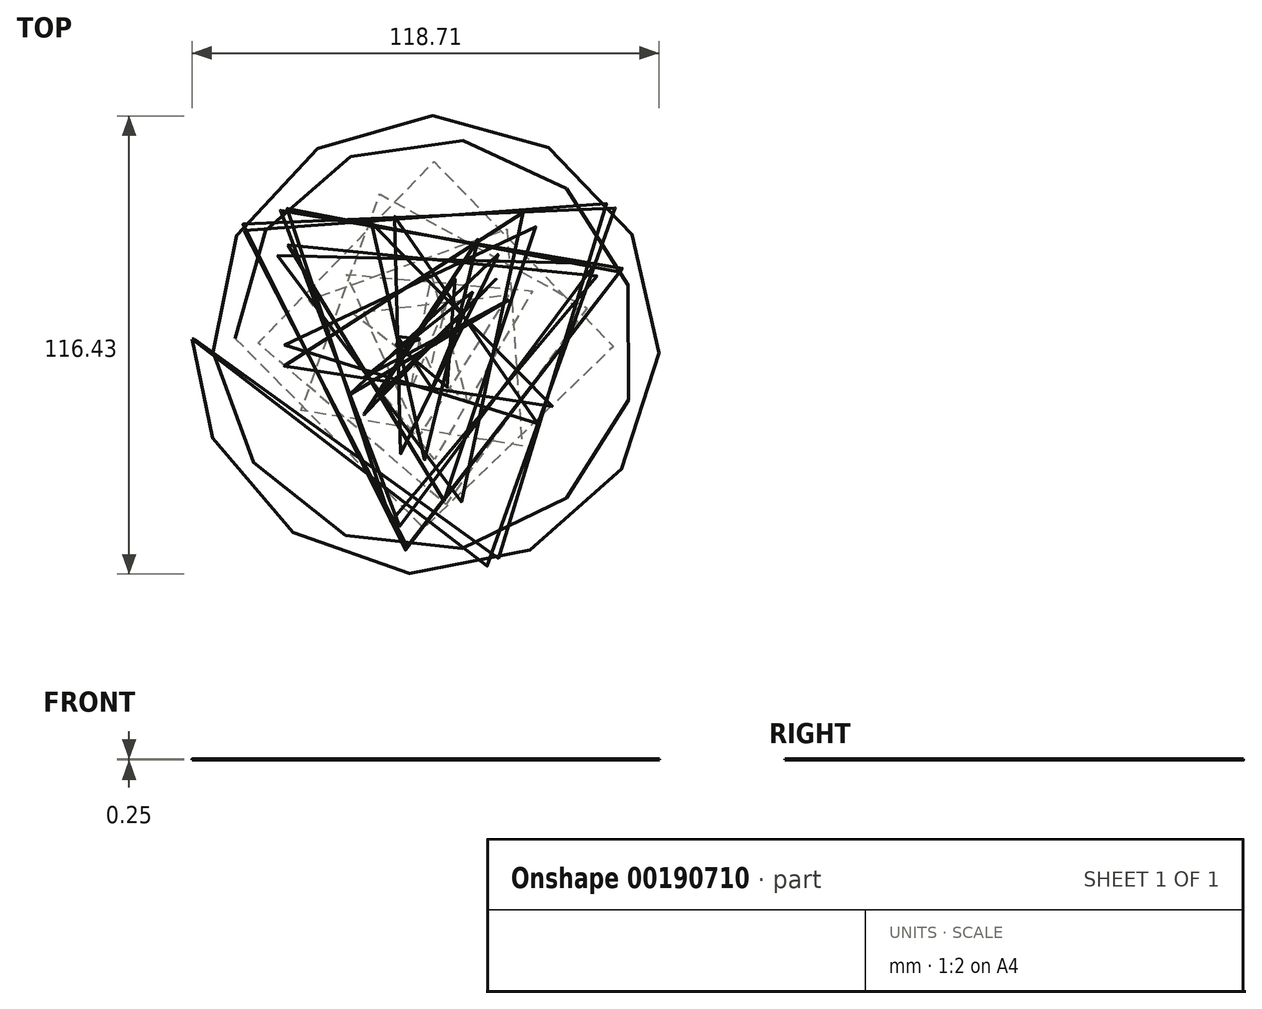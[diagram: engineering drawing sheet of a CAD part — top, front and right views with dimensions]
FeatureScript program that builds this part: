
annotation { "Feature Type Name" : "Feature", "Feature Type Description" : "" }
export const myFeature = defineFeature(function(context is Context, id is Id, definition is map)
    precondition{}
    {
        {
            var Q0;
            Q0=qCreatedBy(makeId("Top.planeOp"),FACE);
            cPlane(context, id + "F0", {"entities" : qUnion([Q0]), "cplaneType" : CPlaneType.OFFSET, "offset" : 25 * mm, "width" : 150 * mm, "height" : 150 * mm});
        }
        {
            var Q0;
            Q0=qCreatedBy(makeId("Top.planeOp"),FACE);
            var sketch = newSketch(context, id + "F1", { "sketchPlane" : qUnion([Q0])});
            skCircle(sketch, "E0", {"center": v(0, 0) * mm, "radius": 60 * mm});
            skSolve(sketch);
        }
        {
            var Q0;
            Q0=qCreatedBy(id+"F0.planeOp",FACE);
            var sketch = newSketch(context, id + "F2", { "sketchPlane" : qUnion([Q0])});
            skCircle(sketch, "E1", {"center": v(0, 0) * mm, "radius": 2.5 * mm});
            skSolve(sketch);
        }
        {
            var Q0;
            Q0=qCreatedBy(makeId("Top.planeOp"),FACE);
            var sketch = newSketch(context, id + "F3", { "sketchPlane" : qUnion([Q0])});
            skFitSpline(sketch, "E2.0", {"points": [v(-2.5, 0) * mm, v(-2.54, 0.1) * mm, v(-2.57, 0.2) * mm, v(-2.62, 0.43) * mm, v(-2.63, 0.54) * mm, v(-2.65, 0.78) * mm, v(-2.65, 0.9) * mm, v(-2.64, 1.14) * mm, v(-2.62, 1.27) * mm, v(-2.58, 1.51) * mm, v(-2.54, 1.64) * mm, v(-2.46, 1.89) * mm, v(-2.41, 2.01) * mm, v(-2.3, 2.25) * mm, v(-2.22, 2.37) * mm, v(-2.07, 2.6) * mm, v(-1.98, 2.72) * mm, v(-1.8, 2.93) * mm, v(-1.69, 3.04) * mm, v(-1.47, 3.23) * mm, v(-1.35, 3.33) * mm, v(-1.1, 3.5) * mm, v(-0.96, 3.57) * mm, v(-0.68, 3.71) * mm, v(-0.53, 3.78) * mm, v(-0.22, 3.88) * mm, v(-0.07, 3.93) * mm, v(0.26, 4) * mm, v(0.43, 4.02) * mm, v(0.77, 4.04) * mm, v(0.94, 4.04) * mm, v(1.3, 4.02) * mm, v(1.47, 4) * mm, v(1.82, 3.94) * mm, v(2, 3.9) * mm, v(2.35, 3.78) * mm, v(2.52, 3.71) * mm, v(2.86, 3.55) * mm, v(3.03, 3.46) * mm, v(3.36, 3.25) * mm, v(3.52, 3.14) * mm, v(3.82, 2.88) * mm, v(3.97, 2.75) * mm, v(4.24, 2.45) * mm, v(4.37, 2.3) * mm, v(4.61, 1.96) * mm, v(4.73, 1.78) * mm, v(4.93, 1.4) * mm, v(5.02, 1.21) * mm, v(5.17, 0.81) * mm, v(5.24, 0.6) * mm, v(5.35, 0.18) * mm, v(5.39, -0.04) * mm, v(5.44, -0.49) * mm, v(5.45, -0.72) * mm, v(5.45, -1.18) * mm, v(5.43, -1.4) * mm, v(5.37, -1.87) * mm, v(5.32, -2.1) * mm, v(5.2, -2.56) * mm, v(5.13, -2.8) * mm, v(4.94, -3.24) * mm, v(4.84, -3.46) * mm, v(4.6, -3.9) * mm, v(4.46, -4.1) * mm, v(4.16, -4.51) * mm, v(4, -4.7) * mm, v(3.64, -5.08) * mm, v(3.45, -5.25) * mm, v(3.05, -5.58) * mm, v(2.83, -5.74) * mm, v(2.38, -6.02) * mm, v(2.14, -6.15) * mm, v(1.65, -6.37) * mm, v(1.4, -6.47) * mm, v(0.88, -6.64) * mm, v(0.6, -6.7) * mm, v(0.06, -6.81) * mm, v(-0.22, -6.84) * mm, v(-0.79, -6.88) * mm, v(-1.08, -6.88) * mm, v(-1.65, -6.84) * mm, v(-1.94, -6.8) * mm, v(-2.52, -6.7) * mm, v(-2.8, -6.62) * mm, v(-3.37, -6.43) * mm, v(-3.65, -6.32) * mm, v(-4.2, -6.06) * mm, v(-4.46, -5.92) * mm, v(-4.98, -5.59) * mm, v(-5.23, -5.4) * mm, v(-5.71, -5.01) * mm, v(-5.94, -4.8) * mm, v(-6.37, -4.34) * mm, v(-6.58, -4.1) * mm, v(-6.96, -3.58) * mm, v(-7.13, -3.3) * mm, v(-7.45, -2.74) * mm, v(-7.59, -2.44) * mm, v(-7.84, -1.83) * mm, v(-7.94, -1.51) * mm, v(-8.11, -0.87) * mm, v(-8.18, -0.54) * mm, v(-8.27, 0.13) * mm, v(-8.3, 0.47) * mm, v(-8.3, 1.16) * mm, v(-8.29, 1.5) * mm, v(-8.2, 2.2) * mm, v(-8.15, 2.54) * mm, v(-7.98, 3.23) * mm, v(-7.88, 3.57) * mm, v(-7.62, 4.24) * mm, v(-7.48, 4.56) * mm, v(-7.14, 5.2) * mm, v(-6.95, 5.51) * mm, v(-6.53, 6.11) * mm, v(-6.3, 6.4) * mm, v(-5.8, 6.95) * mm, v(-5.54, 7.22) * mm, v(-4.97, 7.7) * mm, v(-4.67, 7.94) * mm, v(-4.04, 8.36) * mm, v(-3.7, 8.55) * mm, v(-3.02, 8.9) * mm, v(-2.67, 9.05) * mm, v(-1.93, 9.3) * mm, v(-1.56, 9.42) * mm, v(-0.79, 9.59) * mm, v(-0.4, 9.65) * mm, v(0.4, 9.72) * mm, v(0.8, 9.74) * mm, v(1.6, 9.71) * mm, v(2, 9.68) * mm, v(2.81, 9.55) * mm, v(3.21, 9.47) * mm, v(4, 9.24) * mm, v(4.4, 9.1) * mm, v(5.16, 8.78) * mm, v(5.54, 8.6) * mm, v(6.27, 8.17) * mm, v(6.62, 7.93) * mm, v(7.3, 7.42) * mm, v(7.62, 7.14) * mm, v(8.24, 6.54) * mm, v(8.53, 6.22) * mm, v(9.07, 5.54) * mm, v(9.33, 5.18) * mm, v(9.79, 4.44) * mm, v(10, 4.05) * mm, v(10.36, 3.24) * mm, v(10.52, 2.82) * mm, v(10.8, 1.97) * mm, v(10.9, 1.53) * mm, v(11.06, 0.64) * mm, v(11.12, 0.18) * mm, v(11.17, -0.73) * mm, v(11.17, -1.2) * mm, v(11.1, -2.11) * mm, v(11.05, -2.57) * mm, v(10.87, -3.5) * mm, v(10.76, -3.95) * mm, v(10.46, -4.84) * mm, v(10.3, -5.28) * mm, v(9.89, -6.15) * mm, v(9.66, -6.57) * mm, v(9.15, -7.38) * mm, v(8.87, -7.78) * mm, v(8.26, -8.53) * mm, v(7.92, -8.89) * mm, v(7.22, -9.56) * mm, v(6.84, -9.88) * mm, v(6.05, -10.47) * mm, v(5.63, -10.74) * mm, v(4.76, -11.24) * mm, v(4.31, -11.46) * mm, v(3.38, -11.84) * mm, v(2.9, -12) * mm, v(1.93, -12.28) * mm, v(1.43, -12.39) * mm, v(0.41, -12.54) * mm, v(-0.1, -12.58) * mm, v(-1.14, -12.6) * mm, v(-1.66, -12.58) * mm, v(-2.7, -12.48) * mm, v(-3.21, -12.4) * mm, v(-4.24, -12.16) * mm, v(-4.75, -12.01) * mm, v(-5.74, -11.65) * mm, v(-6.24, -11.44) * mm, v(-7.19, -10.96) * mm, v(-7.65, -10.68) * mm, v(-8.55, -10.08) * mm, v(-8.98, -9.75) * mm, v(-9.8, -9.03) * mm, v(-10.2, -8.65) * mm, v(-10.93, -7.83) * mm, v(-11.27, -7.4) * mm, v(-11.9, -6.49) * mm, v(-12.19, -6.01) * mm, v(-12.7, -5.02) * mm, v(-12.94, -4.51) * mm, v(-13.34, -3.46) * mm, v(-13.5, -2.92) * mm, v(-13.77, -1.82) * mm, v(-13.87, -1.25) * mm, v(-14, -0.12) * mm, v(-14.03, 0.46) * mm, v(-14.02, 1.61) * mm, v(-13.98, 2.2) * mm, v(-13.83, 3.34) * mm, v(-13.72, 3.92) * mm, v(-13.42, 5.05) * mm, v(-13.24, 5.6) * mm, v(-12.8, 6.7) * mm, v(-12.55, 7.24) * mm, v(-11.98, 8.29) * mm, v(-11.66, 8.8) * mm, v(-10.96, 9.77) * mm, v(-10.58, 10.23) * mm, v(-9.75, 11.12) * mm, v(-9.31, 11.54) * mm, v(-8.38, 12.32) * mm, v(-7.9, 12.69) * mm, v(-6.86, 13.36) * mm, v(-6.33, 13.66) * mm, v(-5.21, 14.2) * mm, v(-4.64, 14.44) * mm, v(-3.46, 14.84) * mm, v(-2.86, 15) * mm, v(-1.63, 15.27) * mm, v(-1, 15.36) * mm, v(0.25, 15.46) * mm, v(0.89, 15.48) * mm, v(2.16, 15.43) * mm, v(2.8, 15.36) * mm, v(4.06, 15.16) * mm, v(4.69, 15.01) * mm, v(5.93, 14.65) * mm, v(6.54, 14.43) * mm, v(7.73, 13.91) * mm, v(8.31, 13.62) * mm, v(9.44, 12.95) * mm, v(9.99, 12.58) * mm, v(11.03, 11.78) * mm, v(11.53, 11.35) * mm, v(12.48, 10.41) * mm, v(12.92, 9.92) * mm, v(13.75, 8.87) * mm, v(14.14, 8.32) * mm, v(14.84, 7.17) * mm, v(15.15, 6.57) * mm, v(15.57, 5.64) * mm, v(15.83, 5.02) * mm, v(16.16, 4.05) * mm, v(16.43, 3.06) * mm, v(16.65, 2.05) * mm, v(16.8, 1.03) * mm, v(16.89, 0) * mm, v(16.9, -1.04) * mm, v(16.87, -2.08) * mm, v(16.77, -3.12) * mm, v(16.6, -4.16) * mm, v(16.37, -5.18) * mm, v(16.07, -6.2) * mm, v(15.7, -7.2) * mm, v(15.29, -8.17) * mm, v(14.8, -9.12) * mm, v(14.27, -10.05) * mm, v(13.67, -10.94) * mm, v(13.01, -11.8) * mm, v(12.3, -12.6) * mm, v(11.54, -13.38) * mm, v(10.74, -14.1) * mm, v(9.88, -14.79) * mm, v(8.98, -15.41) * mm, v(8.05, -15.99) * mm, v(7.07, -16.5) * mm, v(6.07, -16.96) * mm, v(5.03, -17.35) * mm, v(3.97, -17.68) * mm, v(2.89, -17.95) * mm, v(1.79, -18.15) * mm, v(0.67, -18.28) * mm, v(-0.45, -18.34) * mm, v(-1.58, -18.33) * mm, v(-2.7, -18.26) * mm, v(-3.83, -18.11) * mm, v(-4.95, -17.9) * mm, v(-6.06, -17.61) * mm, v(-7.15, -17.26) * mm, v(-8.22, -16.84) * mm, v(-9.26, -16.35) * mm, v(-10.28, -15.8) * mm, v(-11.26, -15.19) * mm, v(-12.2, -14.51) * mm, v(-13.11, -13.78) * mm, v(-13.98, -12.98) * mm, v(-14.79, -12.14) * mm, v(-15.55, -11.24) * mm, v(-16.26, -10.3) * mm, v(-16.9, -9.3) * mm, v(-17.5, -8.28) * mm, v(-18.03, -7.2) * mm, v(-18.49, -6.1) * mm, v(-18.88, -4.98) * mm, v(-19.2, -3.82) * mm, v(-19.46, -2.64) * mm, v(-19.64, -1.45) * mm, v(-19.75, -0.24) * mm, v(-19.78, 0.97) * mm, v(-19.74, 2.19) * mm, v(-19.63, 3.4) * mm, v(-19.44, 4.61) * mm, v(-19.17, 5.81) * mm, v(-18.83, 7) * mm, v(-18.42, 8.16) * mm, v(-17.93, 9.3) * mm, v(-17.38, 10.41) * mm, v(-16.75, 11.5) * mm, v(-16.06, 12.53) * mm, v(-15.3, 13.53) * mm, v(-14.48, 14.48) * mm, v(-13.6, 15.38) * mm, v(-12.67, 16.23) * mm, v(-11.68, 17.03) * mm, v(-10.65, 17.76) * mm, v(-9.56, 18.43) * mm, v(-8.44, 19.03) * mm, v(-7.27, 19.57) * mm, v(-6.08, 20.03) * mm, v(-4.85, 20.42) * mm, v(-3.6, 20.73) * mm, v(-2.33, 20.97) * mm, v(-1.04, 21.13) * mm, v(0.26, 21.21) * mm, v(1.56, 21.21) * mm, v(2.87, 21.13) * mm, v(4.17, 20.97) * mm, v(5.46, 20.73) * mm, v(6.74, 20.4) * mm, v(8, 20) * mm, v(9.24, 19.53) * mm, v(10.44, 18.98) * mm, v(11.62, 18.35) * mm, v(12.75, 17.65) * mm, v(13.85, 16.88) * mm, v(14.9, 16.04) * mm, v(15.9, 15.13) * mm, v(16.83, 14.16) * mm, v(17.71, 13.14) * mm, v(18.53, 12.06) * mm, v(19.29, 10.93) * mm, v(19.97, 9.75) * mm, v(20.58, 8.53) * mm, v(21.12, 7.27) * mm, v(21.58, 5.97) * mm, v(21.96, 4.65) * mm, v(22.26, 3.3) * mm, v(22.48, 1.94) * mm, v(22.6, 0.56) * mm, v(22.66, -0.83) * mm, v(22.62, -2.23) * mm, v(22.5, -3.62) * mm, v(22.29, -5) * mm, v(22, -6.38) * mm, v(21.61, -7.73) * mm, v(21.15, -9.06) * mm, v(20.6, -10.37) * mm, v(19.98, -11.64) * mm, v(19.27, -12.88) * mm, v(18.5, -14.07) * mm, v(17.64, -15.21) * mm, v(16.71, -16.3) * mm, v(15.72, -17.34) * mm, v(14.66, -18.32) * mm, v(13.54, -19.23) * mm, v(12.37, -20.07) * mm, v(11.14, -20.84) * mm, v(9.86, -21.53) * mm, v(8.55, -22.15) * mm, v(7.19, -22.69) * mm, v(5.8, -23.14) * mm, v(4.38, -23.5) * mm, v(2.93, -23.78) * mm, v(1.47, -23.98) * mm, v(0, -24.08) * mm, v(-1.48, -24.09) * mm, v(-2.96, -24) * mm, v(-4.44, -23.84) * mm, v(-5.9, -23.57) * mm, v(-7.36, -23.22) * mm, v(-8.79, -22.78) * mm, v(-10.19, -22.25) * mm, v(-11.56, -21.63) * mm, v(-12.9, -20.93) * mm, v(-14.19, -20.15) * mm, v(-15.43, -19.28) * mm, v(-16.62, -18.34) * mm, v(-17.76, -17.33) * mm, v(-18.83, -16.24) * mm, v(-19.83, -15.1) * mm, v(-20.77, -13.88) * mm, v(-21.63, -12.6) * mm, v(-22.4, -11.28) * mm, v(-23.11, -9.9) * mm, v(-23.73, -8.5) * mm, v(-24.26, -7.04) * mm, v(-24.7, -5.55) * mm, v(-25.05, -4.03) * mm, v(-25.3, -2.5) * mm, v(-25.46, -0.94) * mm, v(-25.53, 0.63) * mm, v(-25.5, 2.2) * mm, v(-25.37, 3.76) * mm, v(-25.15, 5.32) * mm, v(-24.83, 6.87) * mm, v(-24.42, 8.4) * mm, v(-23.9, 9.9) * mm, v(-23.3, 11.37) * mm, v(-22.61, 12.8) * mm, v(-21.83, 14.2) * mm, v(-20.96, 15.55) * mm, v(-20.01, 16.84) * mm, v(-18.99, 18.07) * mm, v(-17.88, 19.25) * mm, v(-16.7, 20.35) * mm, v(-15.46, 21.38) * mm, v(-14.14, 22.34) * mm, v(-12.78, 23.2) * mm, v(-11.35, 24) * mm, v(-9.88, 24.7) * mm, v(-8.36, 25.32) * mm, v(-6.81, 25.84) * mm, v(-5.22, 26.26) * mm, v(-3.61, 26.59) * mm, v(-1.98, 26.81) * mm, v(-0.33, 26.94) * mm, v(1.32, 26.97) * mm, v(2.98, 26.9) * mm, v(4.63, 26.71) * mm, v(6.28, 26.43) * mm, v(7.9, 26.05) * mm, v(9.5, 25.57) * mm, v(11.08, 25) * mm, v(12.61, 24.32) * mm, v(14.11, 23.54) * mm, v(15.56, 22.68) * mm, v(16.96, 21.73) * mm, v(18.3, 20.69) * mm, v(19.57, 19.57) * mm, v(20.77, 18.37) * mm, v(21.9, 17.1) * mm, v(22.96, 15.75) * mm, v(23.93, 14.34) * mm, v(24.81, 12.88) * mm, v(25.6, 11.35) * mm, v(26.3, 9.78) * mm, v(26.91, 8.16) * mm, v(27.42, 6.51) * mm, v(27.82, 4.83) * mm, v(28.12, 3.12) * mm, v(28.31, 1.4) * mm, v(28.4, -0.35) * mm, v(28.38, -2.1) * mm, v(28.26, -3.84) * mm, v(28.02, -5.57) * mm, v(27.68, -7.3) * mm, v(27.24, -9) * mm, v(26.69, -10.67) * mm, v(26.03, -12.31) * mm, v(25.28, -13.91) * mm, v(24.43, -15.47) * mm, v(23.48, -16.97) * mm, v(22.44, -18.41) * mm, v(21.3, -19.79) * mm, v(20.1, -21.1) * mm, v(18.8, -22.34) * mm, v(17.42, -23.5) * mm, v(15.98, -24.56) * mm, v(14.47, -25.54) * mm, v(12.9, -26.43) * mm, v(11.28, -27.23) * mm, v(9.6, -27.92) * mm, v(7.9, -28.51) * mm, v(6.14, -29) * mm, v(4.36, -29.37) * mm, v(2.55, -29.64) * mm, v(0.73, -29.8) * mm, v(-1.1, -29.84) * mm, v(-2.93, -29.78) * mm, v(-4.76, -29.6) * mm, v(-6.58, -29.3) * mm, v(-8.38, -28.9) * mm, v(-10.15, -28.38) * mm, v(-11.9, -27.76) * mm, v(-13.6, -27.03) * mm, v(-15.26, -26.2) * mm, v(-16.87, -25.25) * mm, v(-18.42, -24.22) * mm, v(-19.9, -23.08) * mm, v(-21.33, -21.86) * mm, v(-22.67, -20.55) * mm, v(-23.93, -19.15) * mm, v(-25.1, -17.68) * mm, v(-26.2, -16.14) * mm, v(-27.18, -14.53) * mm, v(-28.07, -12.86) * mm, v(-28.86, -11.13) * mm, v(-29.54, -9.36) * mm, v(-30.11, -7.54) * mm, v(-30.58, -5.7) * mm, v(-30.92, -3.82) * mm, v(-31.15, -1.92) * mm, v(-31.27, 0) * mm, v(-31.27, 1.92) * mm, v(-31.15, 3.84) * mm, v(-30.9, 5.75) * mm, v(-30.55, 7.65) * mm, v(-30.08, 9.53) * mm, v(-29.49, 11.37) * mm, v(-28.79, 13.18) * mm, v(-27.97, 14.95) * mm, v(-27.05, 16.67) * mm, v(-26.03, 18.33) * mm, v(-24.9, 19.92) * mm, v(-23.67, 21.45) * mm, v(-22.35, 22.9) * mm, v(-20.94, 24.27) * mm, v(-19.45, 25.56) * mm, v(-17.87, 26.75) * mm, v(-16.23, 27.84) * mm, v(-14.51, 28.83) * mm, v(-12.74, 29.72) * mm, v(-10.91, 30.5) * mm, v(-9.04, 31.17) * mm, v(-7.12, 31.72) * mm, v(-5.17, 32.15) * mm, v(-3.2, 32.46) * mm, v(-1.2, 32.65) * mm, v(0.8, 32.72) * mm, v(2.81, 32.67) * mm, v(4.82, 32.49) * mm, v(6.81, 32.19) * mm, v(8.79, 31.76) * mm, v(10.74, 31.22) * mm, v(12.65, 30.55) * mm, v(14.53, 29.77) * mm, v(16.35, 28.87) * mm, v(18.12, 27.86) * mm, v(19.83, 26.74) * mm, v(21.47, 25.52) * mm, v(23.03, 24.2) * mm, v(24.51, 22.77) * mm, v(25.9, 21.26) * mm, v(27.2, 19.67) * mm, v(28.41, 18) * mm, v(29.51, 16.24) * mm, v(30.5, 14.43) * mm, v(31.38, 12.55) * mm, v(32.15, 10.62) * mm, v(32.8, 8.64) * mm, v(33.31, 6.63) * mm, v(33.71, 4.58) * mm, v(33.99, 2.5) * mm, v(34.13, 0.42) * mm, v(34.15, -1.68) * mm, v(34.04, -3.77) * mm, v(33.8, -5.86) * mm, v(33.43, -7.94) * mm, v(32.93, -9.99) * mm, v(32.31, -12) * mm, v(31.57, -14) * mm, v(30.7, -15.93) * mm, v(29.71, -17.8) * mm, v(28.61, -19.63) * mm, v(27.4, -21.38) * mm, v(26.08, -23.06) * mm, v(24.65, -24.65) * mm, v(23.13, -26.16) * mm, v(21.52, -27.57) * mm, v(19.82, -28.89) * mm, v(18.04, -30.1) * mm, v(16.19, -31.2) * mm, v(14.27, -32.18) * mm, v(12.29, -33.05) * mm, v(10.25, -33.8) * mm, v(8.17, -34.41) * mm, v(6.06, -34.9) * mm, v(3.91, -35.27) * mm, v(1.75, -35.5) * mm, v(-0.44, -35.6) * mm, v(-2.62, -35.56) * mm, v(-4.8, -35.38) * mm, v(-6.98, -35.08) * mm, v(-9.13, -34.64) * mm, v(-11.25, -34.07) * mm, v(-13.34, -33.36) * mm, v(-15.39, -32.53) * mm, v(-17.38, -31.58) * mm, v(-19.31, -30.5) * mm, v(-21.18, -29.3) * mm, v(-22.97, -28) * mm, v(-24.68, -26.57) * mm, v(-26.3, -25.05) * mm, v(-27.84, -23.43) * mm, v(-29.27, -21.7) * mm, v(-30.6, -19.9) * mm, v(-31.8, -18.02) * mm, v(-32.9, -16.06) * mm, v(-33.87, -14.03) * mm, v(-34.72, -11.95) * mm, v(-35.44, -9.8) * mm, v(-36.03, -7.63) * mm, v(-36.49, -5.41) * mm, v(-36.8, -3.17) * mm, v(-36.99, -0.9) * mm, v(-37.03, 1.36) * mm, v(-36.93, 3.64) * mm, v(-36.7, 5.9) * mm, v(-36.32, 8.16) * mm, v(-35.8, 10.38) * mm, v(-35.16, 12.58) * mm, v(-34.37, 14.73) * mm, v(-33.45, 16.84) * mm, v(-32.4, 18.88) * mm, v(-31.23, 20.87) * mm, v(-29.94, 22.78) * mm, v(-28.53, 24.6) * mm, v(-27, 26.35) * mm, v(-25.38, 28) * mm, v(-23.65, 29.55) * mm, v(-21.82, 30.99) * mm, v(-19.91, 32.31) * mm, v(-17.92, 33.52) * mm, v(-15.85, 34.61) * mm, v(-13.72, 35.57) * mm, v(-11.53, 36.4) * mm, v(-9.3, 37.1) * mm, v(-7.01, 37.65) * mm, v(-4.7, 38.06) * mm, v(-2.36, 38.33) * mm, v(0, 38.46) * mm, v(2.36, 38.45) * mm, v(4.72, 38.28) * mm, v(7.07, 37.98) * mm, v(9.4, 37.53) * mm, v(11.7, 36.93) * mm, v(13.96, 36.2) * mm, v(16.18, 35.33) * mm, v(18.34, 34.32) * mm, v(20.44, 33.18) * mm, v(22.47, 31.9) * mm, v(24.42, 30.51) * mm, v(26.28, 29) * mm, v(28.05, 27.37) * mm, v(29.72, 25.64) * mm, v(31.28, 23.8) * mm, v(32.73, 21.87) * mm, v(34.05, 19.85) * mm, v(35.26, 17.75) * mm, v(36.33, 15.58) * mm, v(37.27, 13.34) * mm, v(38.07, 11.04) * mm, v(38.73, 8.7) * mm, v(39.25, 6.32) * mm, v(39.62, 3.9) * mm, v(39.84, 1.47) * mm, v(39.91, -0.98) * mm, v(39.83, -3.43) * mm, v(39.6, -5.87) * mm, v(39.22, -8.3) * mm, v(38.7, -10.7) * mm, v(38.02, -13.08) * mm, v(37.2, -15.4) * mm, v(36.23, -17.68) * mm, v(35.13, -19.9) * mm, v(33.89, -22.05) * mm, v(32.52, -24.12) * mm, v(31.02, -26.1) * mm, v(29.4, -28) * mm, v(27.67, -29.78) * mm, v(25.83, -31.47) * mm, v(23.88, -33.04) * mm, v(21.84, -34.49) * mm, v(19.71, -35.81) * mm, v(17.5, -37) * mm, v(15.22, -38.06) * mm, v(12.88, -38.97) * mm, v(10.48, -39.74) * mm, v(8.03, -40.37) * mm, v(5.55, -40.84) * mm, v(3.04, -41.16) * mm, v(0.5, -41.32) * mm, v(-2.03, -41.33) * mm, v(-4.57, -41.19) * mm, v(-7.1, -40.89) * mm, v(-9.6, -40.43) * mm, v(-12.08, -39.82) * mm, v(-14.52, -39.05) * mm, v(-16.9, -38.14) * mm, v(-19.24, -37.08) * mm, v(-21.5, -35.88) * mm, v(-23.7, -34.54) * mm, v(-25.8, -33.07) * mm, v(-27.82, -31.47) * mm, v(-29.74, -29.74) * mm, v(-31.55, -27.9) * mm, v(-33.24, -25.95) * mm, v(-34.82, -23.89) * mm, v(-36.27, -21.74) * mm, v(-37.58, -19.5) * mm, v(-38.76, -17.18) * mm, v(-39.8, -14.8) * mm, v(-40.68, -12.34) * mm, v(-41.41, -9.84) * mm, v(-42, -7.29) * mm, v(-42.42, -4.7) * mm, v(-42.68, -2.1) * mm, v(-42.78, 0.52) * mm, v(-42.73, 3.15) * mm, v(-42.51, 5.77) * mm, v(-42.13, 8.38) * mm, v(-41.6, 10.96) * mm, v(-40.9, 13.5) * mm, v(-40.04, 16.01) * mm, v(-39.04, 18.46) * mm, v(-37.88, 20.85) * mm, v(-36.58, 23.16) * mm, v(-35.13, 25.4) * mm, v(-33.55, 27.54) * mm, v(-31.84, 29.58) * mm, v(-30, 31.52) * mm, v(-28.06, 33.34) * mm, v(-26, 35.04) * mm, v(-23.82, 36.62) * mm, v(-21.56, 38.06) * mm, v(-19.21, 39.36) * mm, v(-16.78, 40.52) * mm, v(-14.29, 41.52) * mm, v(-11.73, 42.38) * mm, v(-9.12, 43.07) * mm, v(-6.47, 43.6) * mm, v(-3.79, 43.97) * mm, v(-1.09, 44.18) * mm, v(1.63, 44.22) * mm, v(4.34, 44.1) * mm, v(7.05, 43.8) * mm, v(9.73, 43.34) * mm, v(12.39, 42.71) * mm, v(15, 41.93) * mm, v(17.57, 40.98) * mm, v(20.07, 39.88) * mm, v(22.5, 38.62) * mm, v(24.86, 37.21) * mm, v(27.13, 35.66) * mm, v(29.3, 33.97) * mm, v(31.37, 32.15) * mm, v(33.33, 30.2) * mm, v(35.16, 28.14) * mm, v(36.87, 25.97) * mm, v(38.44, 23.69) * mm, v(39.87, 21.31) * mm, v(41.15, 18.85) * mm, v(42.28, 16.31) * mm, v(43.25, 13.7) * mm, v(44.07, 11.04) * mm, v(44.72, 8.33) * mm, v(45.2, 5.58) * mm, v(45.51, 2.8) * mm, v(45.65, 0) * mm, v(45.62, -2.8) * mm, v(45.42, -5.6) * mm, v(45.05, -8.39) * mm, v(44.5, -11.15) * mm, v(43.8, -13.87) * mm, v(42.9, -16.55) * mm, v(41.86, -19.17) * mm, v(40.66, -21.73) * mm, v(39.3, -24.21) * mm, v(37.79, -26.61) * mm, v(36.13, -28.91) * mm, v(34.33, -31.11) * mm, v(32.4, -33.2) * mm, v(30.33, -35.16) * mm, v(28.16, -37) * mm, v(25.86, -38.7) * mm, v(23.47, -40.27) * mm, v(20.98, -41.68) * mm, v(18.4, -42.94) * mm, v(15.76, -44.04) * mm, v(13.05, -44.98) * mm, v(10.27, -45.75) * mm, v(7.46, -46.35) * mm, v(4.6, -46.78) * mm, v(1.73, -47.03) * mm, v(-1.16, -47.1) * mm, v(-4.05, -47) * mm, v(-6.93, -46.72) * mm, v(-9.8, -46.26) * mm, v(-12.62, -45.62) * mm, v(-15.42, -44.82) * mm, v(-18.16, -43.84) * mm, v(-20.84, -42.7) * mm, v(-23.44, -41.39) * mm, v(-25.97, -39.92) * mm, v(-28.4, -38.3) * mm, v(-30.73, -36.52) * mm, v(-32.95, -34.61) * mm, v(-35.05, -32.56) * mm, v(-37.03, -30.39) * mm, v(-38.87, -28.1) * mm, v(-40.56, -25.69) * mm, v(-42.11, -23.18) * mm, v(-43.5, -20.58) * mm, v(-44.74, -17.9) * mm, v(-45.8, -15.13) * mm, v(-46.7, -12.3) * mm, v(-47.42, -9.43) * mm, v(-47.97, -6.52) * mm, v(-48.33, -3.57) * mm, v(-48.52, -0.6) * mm, v(-48.52, 2.38) * mm, v(-48.34, 5.36) * mm, v(-47.97, 8.32) * mm, v(-47.43, 11.26) * mm, v(-46.7, 14.16) * mm, v(-45.8, 17.02) * mm, v(-44.72, 19.82) * mm, v(-43.47, 22.55) * mm, v(-42.05, 25.2) * mm, v(-40.47, 27.77) * mm, v(-38.74, 30.23) * mm, v(-36.85, 32.59) * mm, v(-34.83, 34.82) * mm, v(-32.66, 36.94) * mm, v(-30.37, 38.91) * mm, v(-27.96, 40.75) * mm, v(-25.44, 42.44) * mm, v(-22.81, 43.96) * mm, v(-20.1, 45.33) * mm, v(-17.3, 46.53) * mm, v(-14.43, 47.56) * mm, v(-11.5, 48.4) * mm, v(-8.52, 49.08) * mm, v(-5.5, 49.56) * mm, v(-2.45, 49.86) * mm, v(0.61, 49.98) * mm, v(3.68, 49.9) * mm, v(6.74, 49.64) * mm, v(9.78, 49.19) * mm, v(12.8, 48.55) * mm, v(15.76, 47.72) * mm, v(18.68, 46.72) * mm, v(21.54, 45.54) * mm, v(24.32, 44.18) * mm, v(27, 42.65) * mm, v(29.6, 40.96) * mm, v(32.1, 39.11) * mm, v(34.47, 37.11) * mm, v(36.73, 34.97) * mm, v(38.84, 32.69) * mm, v(40.82, 30.28) * mm, v(42.65, 27.75) * mm, v(44.32, 25.1) * mm, v(45.82, 22.37) * mm, v(47.16, 19.54) * mm, v(48.32, 16.63) * mm, v(49.3, 13.65) * mm, v(50.1, 10.6) * mm, v(50.72, 7.52) * mm, v(51.14, 4.4) * mm, v(51.37, 1.26) * mm, v(51.4, -1.9) * mm, v(51.25, -5.05) * mm, v(50.9, -8.19) * mm, v(50.36, -11.3) * mm, v(49.62, -14.39) * mm, v(48.7, -17.42) * mm, v(47.6, -20.4) * mm, v(46.3, -23.3) * mm, v(44.83, -26.13) * mm, v(43.2, -28.86) * mm, v(41.39, -31.49) * mm, v(39.42, -34) * mm, v(37.3, -36.4) * mm, v(35.04, -38.66) * mm, v(32.64, -40.78) * mm, v(30.1, -42.75) * mm, v(27.46, -44.56) * mm, v(24.7, -46.2) * mm, v(21.84, -47.69) * mm, v(18.9, -48.99) * mm, v(15.88, -50.1) * mm, v(12.79, -51.04) * mm, v(9.64, -51.79) * mm, v(6.46, -52.34) * mm, v(3.24, -52.7) * mm, v(0, -52.85) * mm, v(-3.24, -52.8) * mm, v(-6.48, -52.56) * mm, v(-9.7, -52.12) * mm, v(-12.9, -51.48) * mm, v(-16.04, -50.65) * mm, v(-19.14, -49.62) * mm, v(-22.17, -48.4) * mm, v(-25.12, -47) * mm, v(-27.99, -45.42) * mm, v(-30.75, -43.67) * mm, v(-33.4, -41.74) * mm, v(-35.94, -39.66) * mm, v(-38.35, -37.42) * mm, v(-40.61, -35.03) * mm, v(-42.73, -32.5) * mm, v(-44.69, -29.86) * mm, v(-46.48, -27.1) * mm, v(-48.1, -24.22) * mm, v(-49.55, -21.24) * mm, v(-50.81, -18.18) * mm, v(-51.89, -15.05) * mm, v(-52.77, -11.85) * mm, v(-53.45, -8.6) * mm, v(-53.93, -5.31) * mm, v(-54.21, -2) * mm, v(-54.3, 1.33) * mm, v(-54.16, 4.66) * mm, v(-53.83, 7.98) * mm, v(-53.3, 11.28) * mm, v(-52.56, 14.54) * mm, v(-51.62, 17.76) * mm, v(-50.48, 20.91) * mm, v(-49.16, 24) * mm, v(-47.64, 26.99) * mm, v(-45.95, 29.89) * mm, v(-44.07, 32.68) * mm, v(-42.03, 35.36) * mm, v(-39.82, 37.91) * mm, v(-37.46, 40.32) * mm, v(-34.95, 42.59) * mm, v(-32.3, 44.7) * mm, v(-29.54, 46.64) * mm, v(-26.65, 48.41) * mm, v(-23.65, 50) * mm, v(-20.56, 51.41) * mm, v(-17.39, 52.63) * mm, v(-14.14, 53.65) * mm, v(-10.84, 54.48) * mm, v(-7.48, 55.1) * mm, v(-4.1, 55.5) * mm, v(-0.68, 55.7) * mm, v(2.74, 55.7) * mm, v(6.15, 55.48) * mm, v(9.55, 55.06) * mm, v(12.92, 54.42) * mm, v(16.25, 53.58) * mm, v(19.53, 52.54) * mm, v(22.73, 51.3) * mm, v(25.86, 49.85) * mm, v(28.9, 48.22) * mm, v(31.83, 46.4) * mm, v(34.65, 44.4) * mm, v(37.35, 42.24) * mm, v(39.9, 39.91) * mm, v(42.32, 37.43) * mm, v(44.58, 34.8) * mm, v(46.68, 32.03) * mm, v(48.6, 29.13) * mm, v(50.35, 26.12) * mm, v(51.9, 23.01) * mm, v(53.27, 19.8) * mm, v(54.44, 16.52) * mm, v(55.4, 13.16) * mm, v(56.16, 9.75) * mm, v(56.71, 6.3) * mm, v(57.05, 2.8) * mm, v(57.17, -0.7) * mm, v(57.07, -4.2) * mm, v(56.76, -7.7) * mm, v(56.24, -11.19) * mm, v(55.5, -14.63) * mm, v(54.55, -18.02) * mm, v(53.4, -21.35) * mm, v(52.04, -24.61) * mm, v(50.48, -27.78) * mm, v(48.73, -30.86) * mm, v(46.8, -33.82) * mm, v(44.67, -36.66) * mm, v(42.38, -39.37) * mm, v(39.93, -41.93) * mm, v(37.32, -44.35) * mm, v(34.56, -46.6) * mm, v(31.67, -48.68) * mm, v(28.65, -50.58) * mm, v(25.52, -52.29) * mm, v(22.29, -53.8) * mm, v(18.97, -55.12) * mm, v(15.56, -56.24) * mm, v(12.1, -57.14) * mm, v(8.58, -57.83) * mm, v(5.02, -58.3) * mm, v(1.44, -58.56) * mm, v(-2.16, -58.6) * mm, v(-5.75, -58.4) * mm, v(-9.33, -58) * mm, v(-12.88, -57.37) * mm, v(-16.4, -56.53) * mm, v(-19.85, -55.47) * mm, v(-23.23, -54.2) * mm, v(-26.54, -52.72) * mm, v(-29.75, -51.05) * mm, v(-32.85, -49.17) * mm, v(-35.84, -47.11) * mm, v(-38.7, -44.87) * mm, v(-41.42, -42.45) * mm, v(-43.98, -39.87) * mm, v(-46.4, -37.13) * mm, v(-48.63, -34.25) * mm, v(-50.68, -31.23) * mm, v(-52.55, -28.1) * mm, v(-54.23, -24.84) * mm, v(-55.7, -21.49) * mm, v(-56.97, -18.05) * mm, v(-58.02, -14.53) * mm, v(-58.86, -10.96) * mm, v(-59.47, -7.34) * mm, v(-59.87, -3.68) * mm, v(-59.98, -1.23) * mm, v(-60, 0) * mm]});
            skFitSpline(sketch, "E3.0", {"points": [v(-2.97, -0.17) * mm, v(-3.15, 0.32) * mm, v(-3.23, 1.2) * mm, v(-2.84, 2.36) * mm, v(-2.3, 3.18) * mm, v(-1.53, 3.86) * mm, v(-0.56, 4.34) * mm, v(0.55, 4.58) * mm, v(1.74, 4.51) * mm, v(2.92, 4.14) * mm, v(4.02, 3.44) * mm, v(4.94, 2.46) * mm, v(5.61, 1.23) * mm, v(5.97, -0.2) * mm, v(5.96, -1.7) * mm, v(5.56, -3.22) * mm, v(4.77, -4.64) * mm, v(3.62, -5.86) * mm, v(2.15, -6.78) * mm, v(0.45, -7.32) * mm, v(-1.4, -7.43) * mm, v(-3.26, -7.08) * mm, v(-5.02, -6.25) * mm, v(-6.58, -4.97) * mm, v(-7.8, -3.31) * mm, v(-8.6, -1.35) * mm, v(-8.9, 0.8) * mm, v(-8.64, 3.02) * mm, v(-7.84, 5.15) * mm, v(-6.5, 7.07) * mm, v(-4.7, 8.64) * mm, v(-2.5, 9.74) * mm, v(-0.07, 10.29) * mm, v(2.5, 10.22) * mm, v(5, 9.5) * mm, v(7.32, 8.17) * mm, v(9.27, 6.27) * mm, v(10.73, 3.9) * mm, v(11.59, 1.2) * mm, v(11.76, -1.68) * mm, v(11.2, -4.58) * mm, v(9.94, -7.3) * mm, v(8.01, -9.67) * mm, v(5.52, -11.53) * mm, v(2.6, -12.75) * mm, v(-0.6, -13.23) * mm, v(-3.86, -12.9) * mm, v(-7, -11.77) * mm, v(-9.8, -9.88) * mm, v(-12.1, -7.32) * mm, v(-13.74, -4.22) * mm, v(-14.58, -0.77) * mm, v(-14.55, 2.84) * mm, v(-13.63, 6.4) * mm, v(-11.84, 9.66) * mm, v(-9.28, 12.43) * mm, v(-6.07, 14.52) * mm, v(-2.4, 15.78) * mm, v(1.54, 16.12) * mm, v(5.49, 15.47) * mm, v(9.2, 13.86) * mm, v(12.47, 11.36) * mm, v(15.06, 8.1) * mm, v(16.8, 4.25) * mm, v(17.55, 0.05) * mm, v(17.25, -4.28) * mm, v(15.9, -8.45) * mm, v(13.54, -12.2) * mm, v(10.3, -15.32) * mm, v(6.34, -17.58) * mm, v(1.9, -18.82) * mm, v(-2.76, -18.94) * mm, v(-7.37, -17.9) * mm, v(-11.64, -15.76) * mm, v(-15.3, -12.6) * mm, v(-18.1, -8.6) * mm, v(-19.87, -4) * mm, v(-20.48, 0.96) * mm, v(-19.85, 5.98) * mm, v(-18, 10.74) * mm, v(-15, 14.95) * mm, v(-11.04, 18.34) * mm, v(-6.32, 20.7) * mm, v(-1.11, 21.83) * mm, v(4.27, 21.67) * mm, v(9.5, 20.19) * mm, v(14.27, 17.45) * mm, v(18.26, 13.6) * mm, v(21.23, 8.84) * mm, v(22.96, 3.45) * mm, v(23.34, -2.26) * mm, v(22.3, -7.94) * mm, v(19.9, -13.25) * mm, v(16.23, -17.85) * mm, v(11.52, -21.46) * mm, v(6.01, -23.84) * mm, v(0.04, -24.8) * mm, v(-6.05, -24.3) * mm, v(-11.88, -22.3) * mm, v(-17.1, -18.91) * mm, v(-21.36, -14.32) * mm, v(-24.42, -8.78) * mm, v(-26.04, -2.6) * mm, v(-26.12, 3.84) * mm, v(-24.61, 10.16) * mm, v(-21.59, 15.97) * mm, v(-17.2, 20.9) * mm, v(-11.7, 24.67) * mm, v(-5.4, 27) * mm, v(1.33, 27.73) * mm, v(8.09, 26.8) * mm, v(14.47, 24.22) * mm, v(20.09, 20.14) * mm, v(24.57, 14.77) * mm, v(27.64, 8.42) * mm, v(29.08, 1.46) * mm, v(28.8, -5.7) * mm, v(26.75, -12.61) * mm, v(23.06, -18.88) * mm, v(17.92, -24.1) * mm, v(11.6, -27.94) * mm, v(4.5, -30.15) * mm, v(-2.98, -30.56) * mm, v(-10.4, -29.14) * mm, v(-17.28, -25.93) * mm, v(-23.24, -21.1) * mm, v(-27.87, -14.93) * mm, v(-30.88, -7.77) * mm, v(-32.07, -0.03) * mm, v(-31.34, 7.82) * mm, v(-28.7, 15.3) * mm, v(-24.29, 21.97) * mm, v(-18.35, 27.4) * mm, v(-11.22, 31.25) * mm, v(-3.3, 33.27) * mm, v(4.9, 33.3) * mm, v(12.94, 31.32) * mm, v(20.3, 27.42) * mm, v(26.52, 21.8) * mm, v(31.23, 14.8) * mm, v(34.12, 6.82) * mm, v(34.98, -1.69) * mm, v(33.74, -10.2) * mm, v(30.44, -18.2) * mm, v(25.27, -25.22) * mm, v(18.5, -30.8) * mm, v(10.53, -34.59) * mm, v(1.82, -36.34) * mm, v(-7.11, -35.91) * mm, v(-15.72, -33.31) * mm, v(-23.49, -28.67) * mm, v(-29.93, -22.24) * mm, v(-34.65, -14.39) * mm, v(-37.33, -5.57) * mm, v(-37.79, 3.7) * mm, v(-35.97, 12.84) * mm, v(-31.96, 21.32) * mm, v(-25.98, 28.62) * mm, v(-18.35, 34.27) * mm, v(-9.53, 37.92) * mm, v(-0.03, 39.33) * mm, v(9.58, 38.38) * mm, v(18.73, 35.1) * mm, v(26.85, 29.67) * mm, v(33.44, 22.38) * mm, v(38.09, 13.66) * mm, v(40.5, 4.02) * mm, v(40.48, -5.97) * mm, v(38.02, -15.72) * mm, v(33.25, -24.62) * mm, v(26.41, -32.14) * mm, v(17.9, -37.8) * mm, v(8.23, -41.24) * mm, v(-2.04, -42.23) * mm, v(-12.31, -40.68) * mm, v(-21.94, -36.67) * mm, v(-30.36, -30.4) * mm, v(-37.03, -22.23) * mm, v(-41.54, -12.63) * mm, v(-43.59, -2.17) * mm, v(-43.03, 8.53) * mm, v(-39.87, 18.83) * mm, v(-34.28, 28.1) * mm, v(-26.56, 35.76) * mm, v(-17.16, 41.36) * mm, v(-6.63, 44.51) * mm, v(4.4, 45.01) * mm, v(15.29, 42.8) * mm, v(25.36, 38) * mm, v(34, 30.85) * mm, v(40.68, 21.77) * mm, v(44.97, 11.3) * mm, v(46.6, 0.03) * mm, v(45.42, -11.35) * mm, v(41.5, -22.15) * mm, v(35.04, -31.72) * mm, v(26.41, -39.48) * mm, v(16.1, -44.93) * mm, v(4.73, -47.72) * mm, v(-7.04, -47.66) * mm, v(-18.5, -44.73) * mm, v(-28.95, -39.08) * mm, v(-37.75, -31.02) * mm, v(-44.36, -21.01) * mm, v(-48.36, -9.65) * mm, v(-49.48, 2.4) * mm, v(-47.63, 14.42) * mm, v(-42.9, 25.68) * mm, v(-35.53, 35.5) * mm, v(-25.96, 43.26) * mm, v(-14.74, 48.48) * mm, v(-2.53, 50.84) * mm, v(9.95, 50.15) * mm, v(21.93, 46.44) * mm, v(32.7, 39.9) * mm, v(41.6, 30.88) * mm, v(48.06, 19.94) * mm, v(51.7, 7.7) * mm, v(52.24, -5.12) * mm, v(49.64, -17.73) * mm, v(44.04, -29.4) * mm, v(35.73, -39.38) * mm, v(25.2, -47.08) * mm, v(13.06, -52) * mm, v(0.03, -53.85) * mm, v(-13.11, -52.46) * mm, v(-25.57, -47.9) * mm, v(-36.6, -40.42) * mm, v(-45.51, -30.44) * mm, v(-51.76, -18.55) * mm, v(-54.94, -5.44) * mm, v(-54.84, 8.1) * mm, v(-51.44, 21.28) * mm, v(-44.9, 33.27) * mm, v(-35.62, 43.36) * mm, v(-24.12, 50.92) * mm, v(-11.06, 55.48) * mm, v(2.76, 56.73) * mm, v(16.53, 54.58) * mm, v(29.41, 49.12) * mm, v(40.63, 40.66) * mm, v(49.48, 29.7) * mm, v(55.43, 16.84) * mm, v(58.09, 2.88) * mm, v(57.27, -11.36) * mm, v(53, -25.04) * mm, v(45.5, -37.3) * mm, v(35.2, -47.43) * mm, v(22.72, -54.77) * mm, v(8.76, -58.87) * mm, v(-5.83, -59.46) * mm, v(-20.18, -56.48) * mm, v(-33.43, -50.07) * mm, v(-44.76, -40.6) * mm, v(-53.48, -28.62) * mm, v(-59.05, -14.82) * mm, v(-60.42, -4.96) * mm, v(-60.5, 0) * mm]});
            skLineSegment(sketch, "E4", {"start": v(-60, 0) * mm, "end": v(-60.5, 0) * mm});
            skLineSegment(sketch, "E5", {"start": v(-2.5, 0) * mm, "end": v(-2.97, -0.17) * mm});
            skSolve(sketch);
        }
        {
            var Q0;
            Q0=makeQuery(id+"F3.imprint","IMPRINT",FACE,{"disambiguationData":[TD([[makeQuery(id+"F3.imprint","IMPRINT",EDGE,{"derivedFrom":sQuery(id+"F3.wireOp",EDGE,"E2.0")}),1.0]])]});
            extrude(context, id + "F4", {"entities" : qUnion([Q0]), "depth" : .25 * mm});
        }
    });
